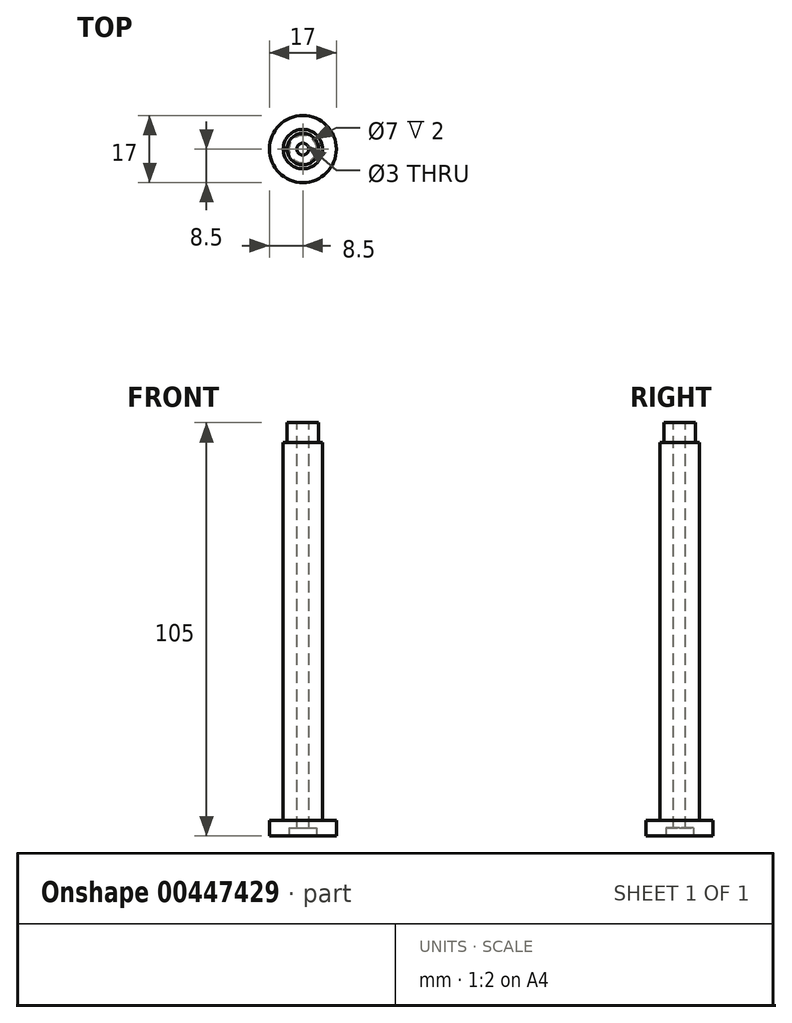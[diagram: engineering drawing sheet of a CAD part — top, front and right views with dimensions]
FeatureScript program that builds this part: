
annotation { "Feature Type Name" : "Feature", "Feature Type Description" : "" }
export const myFeature = defineFeature(function(context is Context, id is Id, definition is map)
    precondition{}
    {
        {
            var Q0;
            Q0=qCreatedBy(makeId("Top.planeOp"),FACE);
            var sketch = newSketch(context, id + "F0", { "sketchPlane" : qUnion([Q0])});
            skCircle(sketch, "E0", {"center": v(0, 0) * mm, "radius": 8.5 * mm});
            skSolve(sketch);
        }
        {
            var Q0;
            Q0=qSketchRegion(id+"F0",true);
            extrude(context, id + "F1", {"entities" : qUnion([Q0]), "depth" : 4 * mm});
        }
        {
            var Q0;
            Q0=qCreatedBy(makeId("Top.planeOp"),FACE);
            var sketch = newSketch(context, id + "F2", { "sketchPlane" : qUnion([Q0])});
            skCircle(sketch, "E1", {"center": v(0, 0) * mm, "radius": 5 * mm});
            skSolve(sketch);
        }
        {
            var Q0;
            Q0=qSketchRegion(id+"F2",true);
            extrude(context, id + "F3", {"entities" : qUnion([Q0]), "operationType" : NewBodyOperationType.ADD, "depth" : 100 * mm});
        }
        {
            var Q0;
            Q0=qCreatedBy(makeId("Right.planeOp"),FACE);
            var sketch = newSketch(context, id + "F4", { "sketchPlane" : qUnion([Q0])});
            skLineSegment(sketch, "E2.bottom", {"start": v(0, 105) * mm, "end": v(4, 105) * mm});
            skLineSegment(sketch, "E2.top", {"start": v(0, 100) * mm, "end": v(4, 100) * mm});
            skLineSegment(sketch, "E2.left", {"start": v(0, 105) * mm, "end": v(0, 100) * mm});
            skLineSegment(sketch, "E2.right", {"start": v(4, 105) * mm, "end": v(4, 100) * mm});
            skSolve(sketch);
        }
        {
            var Q0;
            Q0=makeQuery(id+"F4.imprint","IMPRINT",FACE,{"disambiguationData":[TD([[makeQuery(id+"F4.imprint","IMPRINT",EDGE,{"derivedFrom":sQuery(id+"F4.wireOp",EDGE,"E2.bottom")}),-1.0]])]});
            var Q1;
            Q1=sQuery(id+"F4.wireOp",EDGE,"E2.left");
            revolve(context, id + "F5", {"operationType" : NewBodyOperationType.ADD, "entities" : qUnion([Q0]), "axis" : qUnion([Q1]), "revolveType" : RevolveType.FULL});
        }
        {
            var Q0;
            Q0=makeQuery(id+"F1.opExtrude","CAP_FACE",FACE,{"disambiguationData":[OSD([sQuery(id+"F0.wireOp",EDGE,"E0")])],"isStart":true});
            var sketch = newSketch(context, id + "F6", { "sketchPlane" : qUnion([Q0])});
            skCircle(sketch, "E3", {"center": v(0, 0) * mm, "radius": 3.5 * mm});
            skSolve(sketch);
        }
        {
            var Q0;
            Q0=makeQuery(id+"F6.imprint","IMPRINT",FACE,{"disambiguationData":[TD([[makeQuery(id+"F6.imprint","IMPRINT",EDGE,{"derivedFrom":sQuery(id+"F6.wireOp",EDGE,"E3")}),1.0]])]});
            extrude(context, id + "F7", {"entities" : qUnion([Q0]), "operationType" : NewBodyOperationType.REMOVE, "oppositeDirection" : true, "depth" : 2 * mm});
        }
        {
            var Q0;
            Q0=makeQuery(id+"F5.opRevolve","SWEPT_FACE",FACE,{"disambiguationData":[OSD([sQuery(id+"F4.wireOp",EDGE,"E2.bottom")])]});
            var sketch = newSketch(context, id + "F8", { "sketchPlane" : qUnion([Q0])});
            skCircle(sketch, "E4", {"center": v(0, 0) * mm, "radius": 1.5 * mm});
            skSolve(sketch);
        }
        {
            var Q0;
            Q0 = qSketchRegion(id + "F8", true);
            extrude(context, id + "F9", {"entities" : qUnion([Q0]), "operationType" : NewBodyOperationType.REMOVE, "oppositeDirection" : true, "depth" : 118.6 * mm});
        }
    });
